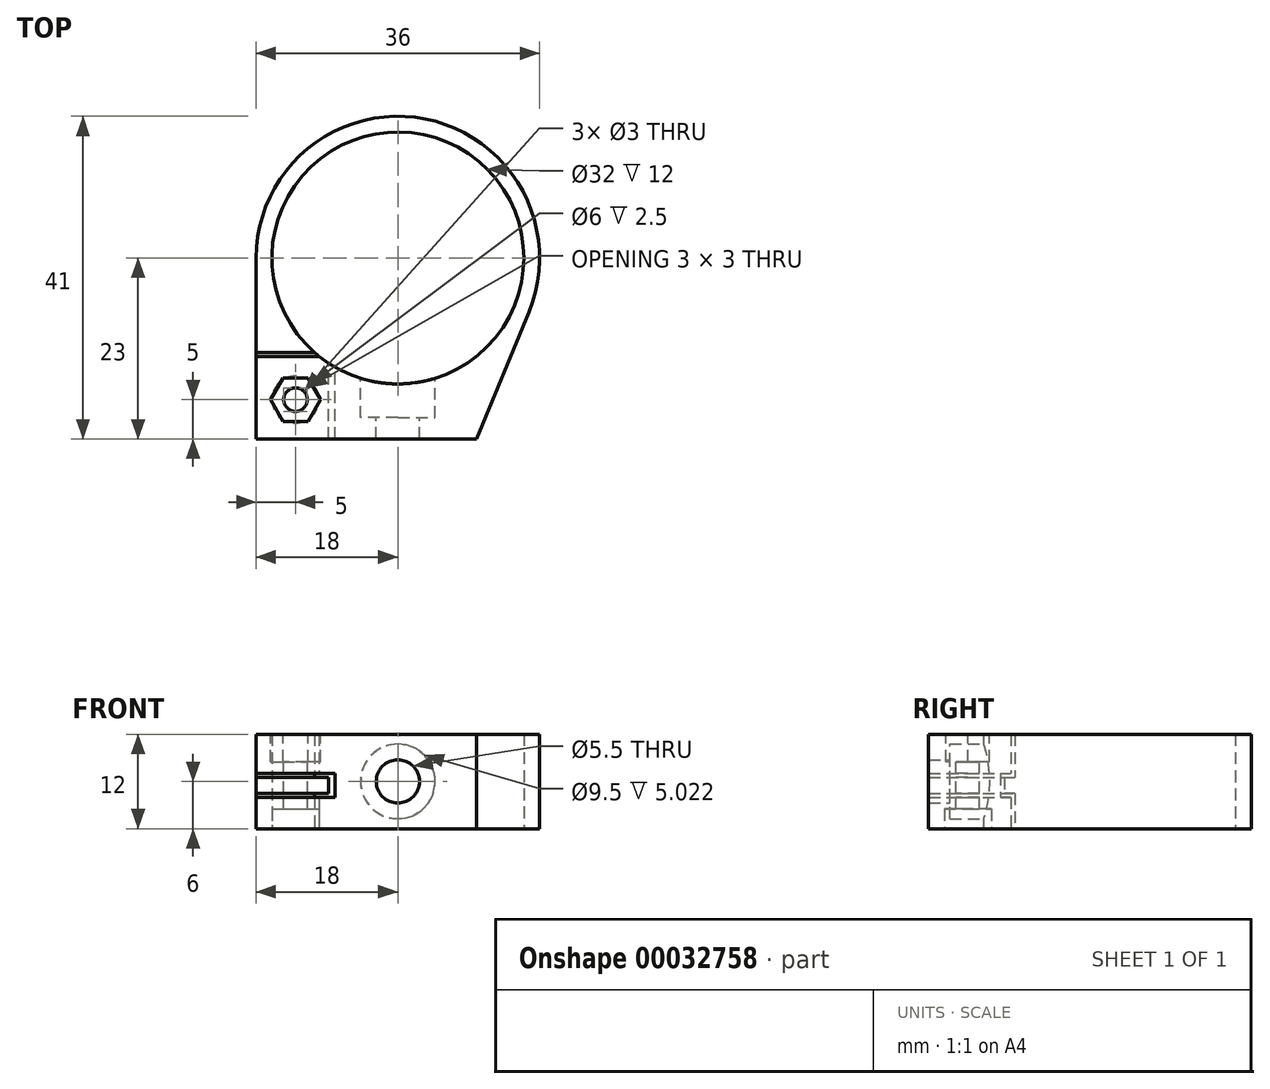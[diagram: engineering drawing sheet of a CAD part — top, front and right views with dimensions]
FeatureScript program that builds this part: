
annotation { "Feature Type Name" : "Feature", "Feature Type Description" : "" }
export const myFeature = defineFeature(function(context is Context, id is Id, definition is map)
    precondition{}
    {
        {
            var Q0;
            Q0=qCreatedBy(makeId("Top.planeOp"),FACE);
            var sketch = newSketch(context, id + "F0", { "sketchPlane" : qUnion([Q0])});
            skCircle(sketch, "E0", {"center": v(0, 0) * mm, "radius": 15 * mm, "construction": true});
            skCircle(sketch, "E1", {"center": v(0, 0) * mm, "radius": 16 * mm});
            skArc(sketch, "E2", {"start": v(16.65, -6.85) * mm, "mid": v(3.5, 17.66) * mm, "end": v(-18, 0) * mm});
            skLineSegment(sketch, "E3", {"start": v(-18, 0) * mm, "end": v(-18, -23) * mm});
            skLineSegment(sketch, "E4", {"start": v(10, -23) * mm, "end": v(16.65, -6.85) * mm});
            skLineSegment(sketch, "E5", {"start": v(-18, -23) * mm, "end": v(10, -23) * mm});
            skSolve(sketch);
        }
        {
            var Q0;
            Q0 = qSketchRegion(id + "F0", true);
            extrude(context, id + "F1", {"entities" : qUnion([Q0]), "depth" : 6 * mm, "hasSecondDirection" : true, "secondDirectionOppositeDirection" : true, "secondDirectionDepth" : 6 * mm});
        }
        {
            var Q0;
            Q0=qCreatedBy(makeId("Front.planeOp"),FACE);
            cPlane(context, id + "F2", {"entities" : qUnion([Q0]), "cplaneType" : CPlaneType.OFFSET, "offset" : 12 * mm, "width" : 150 * mm, "height" : 150 * mm});
        }
        {
            var Q0;
            Q0=qCreatedBy(id+"F2.planeOp",FACE);
            var sketch = newSketch(context, id + "F3", { "sketchPlane" : qUnion([Q0])});
            skLineSegment(sketch, "E6", {"start": v(-18, -1.5) * mm, "end": v(-8.8, -1.5) * mm});
            skLineSegment(sketch, "E7", {"start": v(-8.8, -1.5) * mm, "end": v(-8.8, 0.5) * mm});
            skLineSegment(sketch, "E8", {"start": v(-8.8, 0.5) * mm, "end": v(-18, 0.5) * mm});
            skLineSegment(sketch, "E9", {"start": v(-18, -1.5) * mm, "end": v(-18, -2) * mm});
            skLineSegment(sketch, "E10", {"start": v(-18, -2) * mm, "end": v(-8, -2) * mm});
            skLineSegment(sketch, "E11", {"start": v(-8, -2) * mm, "end": v(-8, 1) * mm});
            skLineSegment(sketch, "E12", {"start": v(-8, 1) * mm, "end": v(-18, 1) * mm});
            skLineSegment(sketch, "E13", {"start": v(-18, 1) * mm, "end": v(-18, 0.5) * mm});
            skSolve(sketch);
        }
        {
            var Q0;
            Q0 = qSketchRegion(id + "F3", true);
            extrude(context, id + "F4", {"entities" : qUnion([Q0]), "operationType" : NewBodyOperationType.REMOVE, "depth" : 25 * mm});
        }
        {
            var Q0;
            Q0=makeQuery(id+"F1.opExtrude","SWEPT_FACE",FACE,{"disambiguationData":[OSD([sQuery(id+"F0.wireOp",EDGE,"E3")])]});
            var sketch = newSketch(context, id + "F5", { "sketchPlane" : qUnion([Q0])});
            skLineSegment(sketch, "E14.bottom", {"start": v(12, -2) * mm, "end": v(12.5, -2) * mm});
            skLineSegment(sketch, "E14.top", {"start": v(12, -6) * mm, "end": v(12.5, -6) * mm});
            skLineSegment(sketch, "E14.left", {"start": v(12, -2) * mm, "end": v(12, -6) * mm});
            skLineSegment(sketch, "E14.right", {"start": v(12.5, -2) * mm, "end": v(12.5, -6) * mm});
            skLineSegment(sketch, "E15.bottom", {"start": v(12, 1) * mm, "end": v(12.5, 1) * mm});
            skLineSegment(sketch, "E15.top", {"start": v(12, 6) * mm, "end": v(12.5, 6) * mm});
            skLineSegment(sketch, "E15.left", {"start": v(12, 1) * mm, "end": v(12, 6) * mm});
            skLineSegment(sketch, "E15.right", {"start": v(12.5, 1) * mm, "end": v(12.5, 6) * mm});
            skSolve(sketch);
        }
        {
            var Q0;
            Q0 = qSketchRegion(id + "F5", true);
            extrude(context, id + "F6", {"entities" : qUnion([Q0]), "operationType" : NewBodyOperationType.REMOVE, "endBound" : BoundingType.UP_TO_NEXT, "oppositeDirection" : true, "depth" : 25 * mm});
        }
        {
            var Q0;
            Q0=makeQuery(id+"F1.opExtrude","CAP_FACE",FACE,{"disambiguationData":[OSD([sQuery(id+"F0.wireOp",EDGE,"E1"),sQuery(id+"F0.wireOp",EDGE,"E2"),sQuery(id+"F0.wireOp",EDGE,"E3"),sQuery(id+"F0.wireOp",EDGE,"LY6zuVOY-wsG1-tMYY-OEZ4-fVzRadRyssAc"),sQuery(id+"F0.wireOp",EDGE,"fucNie0u-L6Eq-ztMz-J3aG-WTLi07nofqBb"),sQuery(id+"F0.wireOp",EDGE,"E4")])],"isStart":false});
            var sketch = newSketch(context, id + "F7", { "sketchPlane" : qUnion([Q0])});
            skCircle(sketch, "E16.cCircle", {"center": v(-13, -18) * mm, "radius": 2.75 * mm, "construction": true});
            skLineSegment(sketch, "E16.0", {"start": v(-9.82, -18) * mm, "end": v(-11.41, -20.75) * mm});
            skLineSegment(sketch, "E16.1", {"start": v(-11.41, -20.75) * mm, "end": v(-14.59, -20.75) * mm});
            skLineSegment(sketch, "E16.2", {"start": v(-14.59, -20.75) * mm, "end": v(-16.18, -18) * mm});
            skLineSegment(sketch, "E16.3", {"start": v(-16.18, -18) * mm, "end": v(-14.59, -15.25) * mm});
            skLineSegment(sketch, "E16.4", {"start": v(-14.59, -15.25) * mm, "end": v(-11.41, -15.25) * mm});
            skLineSegment(sketch, "E16.5", {"start": v(-11.41, -15.25) * mm, "end": v(-9.82, -18) * mm});
            skPoint(sketch, "E16.0.midPoint", {"position": v(-10.62, -19.37) * mm});
            skSolve(sketch);
        }
        {
            var Q0;
            Q0=sQuery(id+"F7.wireOp",VERTEX,"E16.cCircle.center");
            var Q1;
            Q1=makeQuery(id+"F1.opExtrude","SWEPT_BODY",BODY,{"disambiguationData":[OSD([sQuery(id+"F0.wireOp",EDGE,"E1"),sQuery(id+"F0.wireOp",EDGE,"E2"),sQuery(id+"F0.wireOp",EDGE,"E3"),sQuery(id+"F0.wireOp",EDGE,"LY6zuVOY-wsG1-tMYY-OEZ4-fVzRadRyssAc"),sQuery(id+"F0.wireOp",EDGE,"fucNie0u-L6Eq-ztMz-J3aG-WTLi07nofqBb"),sQuery(id+"F0.wireOp",EDGE,"E4")])]});
            hole(context, id + "F8", {"style" : HoleStyle.SIMPLE, "endStyle" : HoleEndStyle.THROUGH, "holeDiameter" : 3 * mm, "locations" : qUnion([Q0]), "scope" : qUnion([Q1]), "isTappedThrough" : true});
        }
        {
            var Q0;
            Q0 = qSketchRegion(id + "F7", true);
            extrude(context, id + "F9", {"entities" : qUnion([Q0]), "operationType" : NewBodyOperationType.REMOVE, "oppositeDirection" : true, "depth" : 3.5 * mm});
        }
        {
            var Q0;
            Q0=makeQuery(id+"F1.opExtrude","CAP_FACE",FACE,{"disambiguationData":[OSD([sQuery(id+"F0.wireOp",EDGE,"E1"),sQuery(id+"F0.wireOp",EDGE,"E2"),sQuery(id+"F0.wireOp",EDGE,"E3"),sQuery(id+"F0.wireOp",EDGE,"LY6zuVOY-wsG1-tMYY-OEZ4-fVzRadRyssAc"),sQuery(id+"F0.wireOp",EDGE,"fucNie0u-L6Eq-ztMz-J3aG-WTLi07nofqBb"),sQuery(id+"F0.wireOp",EDGE,"E4")])],"isStart":true});
            var sketch = newSketch(context, id + "F10", { "sketchPlane" : qUnion([Q0])});
            skCircle(sketch, "E17", {"center": v(-13, 18) * mm, "radius": 3 * mm});
            skSolve(sketch);
        }
        {
            var Q0;
            Q0 = qSketchRegion(id + "F10", true);
            extrude(context, id + "F11", {"entities" : qUnion([Q0]), "operationType" : NewBodyOperationType.REMOVE, "oppositeDirection" : true, "depth" : 2.5 * mm});
        }
        {
            var Q0;
            Q0=qCreatedBy(makeId("Front.planeOp"),FACE);
            var sketch = newSketch(context, id + "F12", { "sketchPlane" : qUnion([Q0])});
            skPoint(sketch, "E18", {"position": v(0, 0) * mm});
            skSolve(sketch);
        }
        {
            var Q0;
            Q0=sQuery(id+"F12.wireOp",VERTEX,"E18");
            var Q1;
            Q1=makeQuery(id+"F1.opExtrude","SWEPT_BODY",BODY,{"disambiguationData":[OSD([sQuery(id+"F0.wireOp",EDGE,"E1"),sQuery(id+"F0.wireOp",EDGE,"E2"),sQuery(id+"F0.wireOp",EDGE,"E3"),sQuery(id+"F0.wireOp",EDGE,"LY6zuVOY-wsG1-tMYY-OEZ4-fVzRadRyssAc"),sQuery(id+"F0.wireOp",EDGE,"fucNie0u-L6Eq-ztMz-J3aG-WTLi07nofqBb"),sQuery(id+"F0.wireOp",EDGE,"E4")])]});
            hole(context, id + "F13", {"style" : HoleStyle.SIMPLE, "endStyle" : HoleEndStyle.THROUGH, "oppositeDirection" : true, "holeDiameter" : 5.5 * mm, "locations" : qUnion([Q0]), "scope" : qUnion([Q1]), "isTappedThrough" : true});
        }
        {
            var Q0;
            Q0=qCreatedBy(makeId("Front.planeOp"),FACE);
            var sketch = newSketch(context, id + "F14", { "sketchPlane" : qUnion([Q0])});
            skCircle(sketch, "E19", {"center": v(0, 0) * mm, "radius": 4.75 * mm});
            skSolve(sketch);
        }
        {
            var Q0;
            Q0=makeQuery(id+"F14.imprint","IMPRINT",FACE,{"disambiguationData":[TD([[makeQuery(id+"F14.imprint","IMPRINT",EDGE,{"derivedFrom":sQuery(id+"F14.wireOp",EDGE,"E19")}),1.0]])]});
            extrude(context, id + "F15", {"entities" : qUnion([Q0]), "operationType" : NewBodyOperationType.REMOVE, "depth" : 20.3 * mm});
        }
    });
